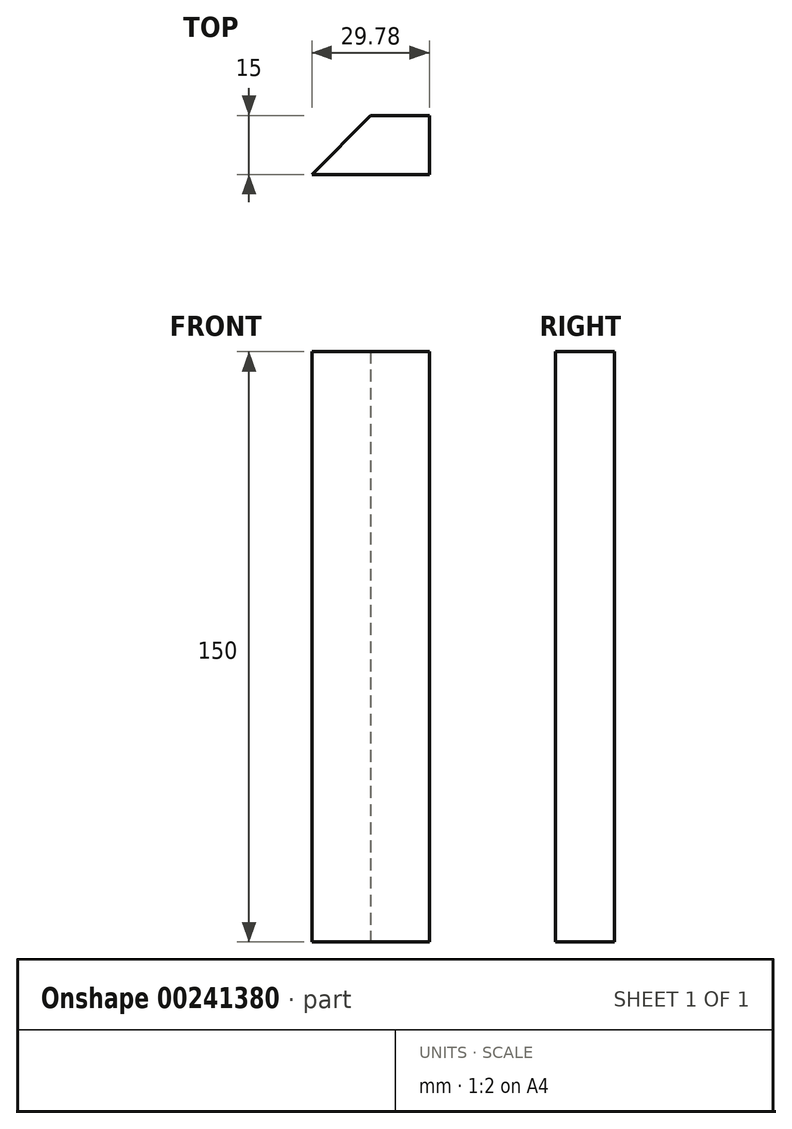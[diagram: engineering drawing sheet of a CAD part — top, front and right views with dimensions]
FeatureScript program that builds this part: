
annotation { "Feature Type Name" : "Feature", "Feature Type Description" : "" }
export const myFeature = defineFeature(function(context is Context, id is Id, definition is map)
    precondition{}
    {
        {
            var Q0;
            Q0=qCreatedBy(makeId("Top.planeOp"),FACE);
            var sketch = newSketch(context, id + "F0", { "sketchPlane" : qUnion([Q0])});
            skLineSegment(sketch, "E0", {"start": v(-22.28, -6.44) * mm, "end": v(-7.5, 8.56) * mm});
            skLineSegment(sketch, "E1", {"start": v(-7.5, 8.56) * mm, "end": v(7.5, 8.56) * mm});
            skLineSegment(sketch, "E2", {"start": v(7.5, 8.56) * mm, "end": v(7.5, -6.44) * mm});
            skLineSegment(sketch, "E3", {"start": v(7.5, -6.44) * mm, "end": v(-22.28, -6.44) * mm});
            skSolve(sketch);
        }
        {
            var Q0;
            Q0 = qSketchRegion(id + "F0", true);
            extrude(context, id + "F1", {"entities" : qUnion([Q0]), "depth" : 150 * mm});
        }
    });
